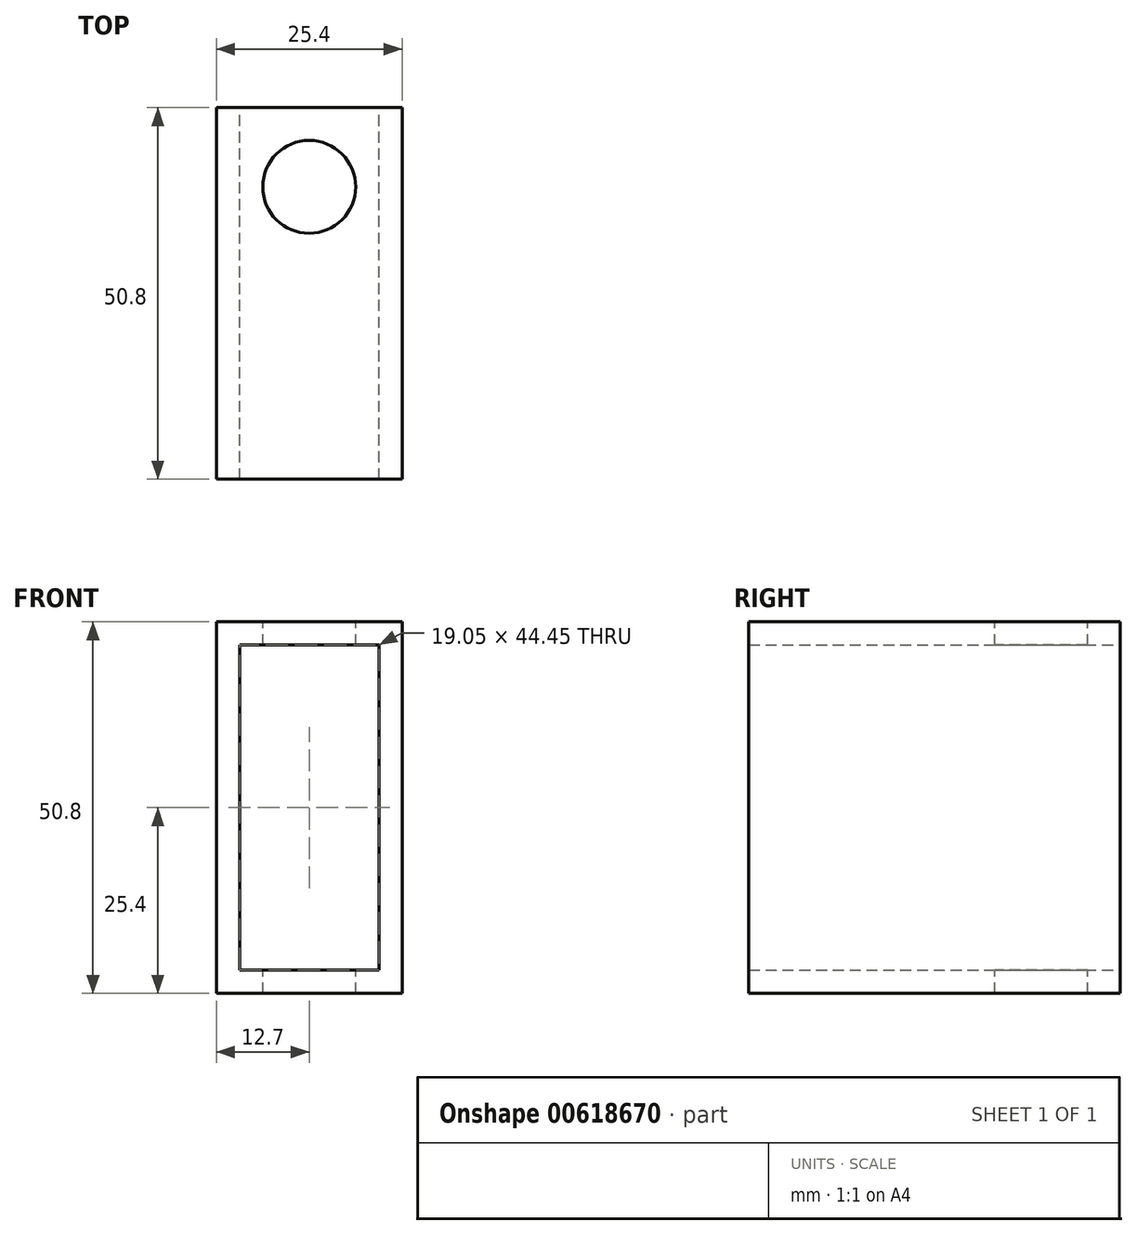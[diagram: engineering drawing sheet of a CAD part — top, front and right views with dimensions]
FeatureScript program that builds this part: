
annotation { "Feature Type Name" : "Feature", "Feature Type Description" : "" }
export const myFeature = defineFeature(function(context is Context, id is Id, definition is map)
    precondition{}
    {
        {
            var Q0;
            Q0=qCreatedBy(makeId("Front.planeOp"),FACE);
            var sketch = newSketch(context, id + "F0", { "sketchPlane" : qUnion([Q0])});
            skLineSegment(sketch, "E0.bottom", {"start": v(0, 0) * mm, "end": v(25.4, 0) * mm});
            skLineSegment(sketch, "E0.top", {"start": v(0, 50.8) * mm, "end": v(25.4, 50.8) * mm});
            skLineSegment(sketch, "E0.left", {"start": v(0, 0) * mm, "end": v(0, 50.8) * mm});
            skLineSegment(sketch, "E0.right", {"start": v(25.4, 0) * mm, "end": v(25.4, 50.8) * mm});
            skLineSegment(sketch, "E1.bottom", {"start": v(3.18, 3.18) * mm, "end": v(22.23, 3.18) * mm});
            skLineSegment(sketch, "E1.top", {"start": v(3.17, 47.63) * mm, "end": v(22.22, 47.63) * mm});
            skLineSegment(sketch, "E1.left", {"start": v(3.17, 3.18) * mm, "end": v(3.17, 47.63) * mm});
            skLineSegment(sketch, "E1.right", {"start": v(22.23, 3.18) * mm, "end": v(22.22, 47.63) * mm});
            skSolve(sketch);
        }
        {
            var Q0;
            Q0=makeQuery(id+"F0.imprint","IMPRINT",FACE,{"disambiguationData":[TD([[makeQuery(id+"F0.imprint","IMPRINT",EDGE,{"derivedFrom":sQuery(id+"F0.wireOp",EDGE,"E0.bottom")}),1.0]])]});
            extrude(context, id + "F1", {"entities" : qUnion([Q0]), "depth" : 50.8 * mm, "offsetDistance" : 25.4 * mm});
        }
        {
            var Q0;
            Q0=makeQuery(id+"F1.opExtrude","SWEPT_FACE",FACE,{"disambiguationData":[OSD([sQuery(id+"F0.wireOp",EDGE,"E0.top")])]});
            var sketch = newSketch(context, id + "F2", { "sketchPlane" : qUnion([Q0])});
            skCircle(sketch, "E2", {"center": v(12.7, -10.84) * mm, "radius": 6.35 * mm});
            skPoint(sketch, "E2.centerSnap0", {"position": v(12.7, 0) * mm});
            skSolve(sketch);
        }
        {
            var Q0;
            Q0=makeQuery(id+"F2.imprint","IMPRINT",FACE,{"disambiguationData":[TD([[makeQuery(id+"F2.imprint","IMPRINT",EDGE,{"derivedFrom":sQuery(id+"F2.wireOp",EDGE,"E2")}),1.0]])]});
            extrude(context, id + "F3", {"entities" : qUnion([Q0]), "operationType" : NewBodyOperationType.REMOVE, "oppositeDirection" : true, "depth" : 50.8 * mm, "offsetDistance" : 25.4 * mm});
        }
    });
